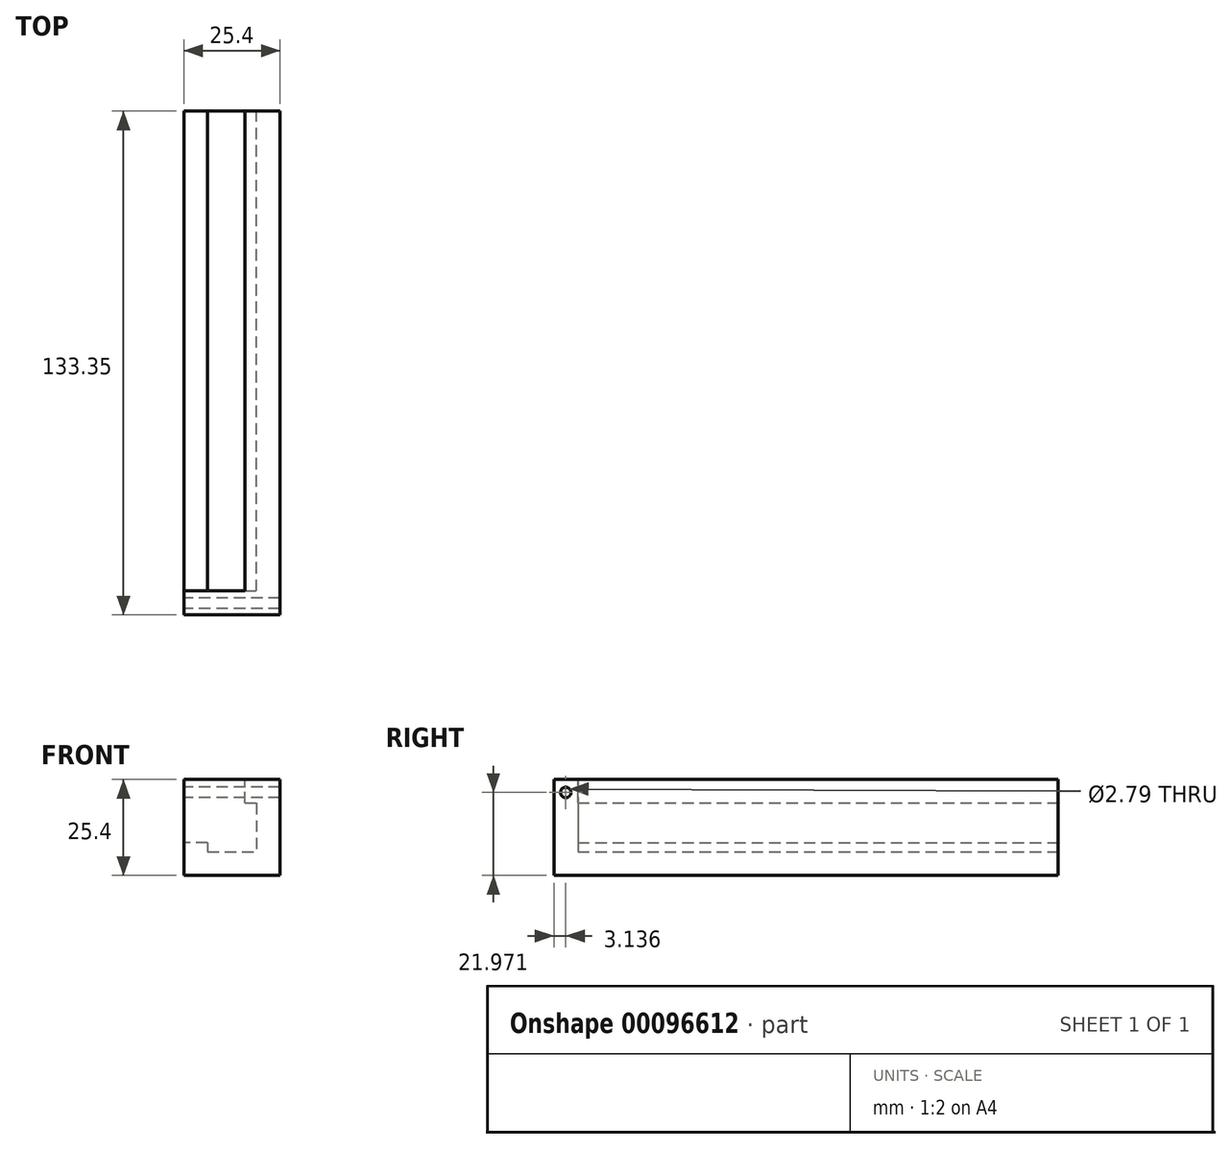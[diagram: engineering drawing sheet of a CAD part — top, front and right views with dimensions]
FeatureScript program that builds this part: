
annotation { "Feature Type Name" : "Feature", "Feature Type Description" : "" }
export const myFeature = defineFeature(function(context is Context, id is Id, definition is map)
    precondition{}
    {
        {
            var Q0;
            Q0=qCreatedBy(makeId("Front.planeOp"),FACE);
            var sketch = newSketch(context, id + "F0", { "sketchPlane" : qUnion([Q0])});
            skLineSegment(sketch, "E0.bottom", {"start": v(-12.7, 12.7) * mm, "end": v(12.7, 12.7) * mm});
            skLineSegment(sketch, "E0.top", {"start": v(-12.7, -12.7) * mm, "end": v(12.7, -12.7) * mm});
            skLineSegment(sketch, "E0.left", {"start": v(-12.7, 12.7) * mm, "end": v(-12.7, -12.7) * mm});
            skLineSegment(sketch, "E0.right", {"start": v(12.7, 12.7) * mm, "end": v(12.7, -12.7) * mm});
            skPoint(sketch, "E0.middle", {"position": v(0, 0) * mm});
            skLineSegment(sketch, "E1.bottom", {"start": v(-6.48, 6.48) * mm, "end": v(6.48, 6.48) * mm});
            skLineSegment(sketch, "E1.top", {"start": v(-6.48, -6.48) * mm, "end": v(6.48, -6.48) * mm});
            skLineSegment(sketch, "E1.left", {"start": v(-6.48, 6.48) * mm, "end": v(-6.48, -6.48) * mm});
            skLineSegment(sketch, "E1.right", {"start": v(6.48, 6.48) * mm, "end": v(6.48, -6.48) * mm});
            skLineSegment(sketch, "E2", {"start": v(3.39, 6.48) * mm, "end": v(3.39, 12.7) * mm});
            skLineSegment(sketch, "E3", {"start": v(3.39, 12.7) * mm, "end": v(3.39, 6.48) * mm});
            skLineSegment(sketch, "E4", {"start": v(-6.48, -4.04) * mm, "end": v(-12.7, -4.04) * mm});
            skLineSegment(sketch, "E5", {"start": v(-12.7, -4.04) * mm, "end": v(-6.48, -4.04) * mm});
            skSolve(sketch);
        }
        {
            var Q0;
            {var subQ3=sQuery(id+"F0.wireOp",EDGE,"E0.top");Q0=makeQuery(id+"F0.imprint","IMPRINT",FACE,{"disambiguationData":[TD([[makeQuery(id+"F0.imprint","IMPRINT",EDGE,{"derivedFrom":subQ3}),1.0]])]});}
            extrude(context, id + "F1", {"entities" : qUnion([Q0]), "depth" : 127 * mm});
        }
        {
            var Q0;
            Q0=makeQuery(id+"F1.opExtrude","CAP_FACE",FACE,{"disambiguationData":[OSD([sQuery(id+"F0.wireOp",EDGE,"E0.bottom"),sQuery(id+"F0.wireOp",EDGE,"E0.top"),sQuery(id+"F0.wireOp",EDGE,"E0.left"),sQuery(id+"F0.wireOp",EDGE,"E0.right"),sQuery(id+"F0.wireOp",EDGE,"E1.bottom"),sQuery(id+"F0.wireOp",EDGE,"E1.top"),sQuery(id+"F0.wireOp",EDGE,"E1.left"),sQuery(id+"F0.wireOp",EDGE,"E1.right"),sQuery(id+"F0.wireOp",EDGE,"E3"),sQuery(id+"F0.wireOp",EDGE,"E5")])],"isStart":false});
            var sketch = newSketch(context, id + "F2", { "sketchPlane" : qUnion([Q0])});
            skLineSegment(sketch, "E6.bottom", {"start": v(12.7, -12.7) * mm, "end": v(-12.7, -12.7) * mm});
            skLineSegment(sketch, "E6.top", {"start": v(12.7, 12.7) * mm, "end": v(-12.7, 12.7) * mm});
            skLineSegment(sketch, "E6.left", {"start": v(12.7, -12.7) * mm, "end": v(12.7, 12.7) * mm});
            skLineSegment(sketch, "E6.right", {"start": v(-12.7, -12.7) * mm, "end": v(-12.7, 12.7) * mm});
            skSolve(sketch);
        }
        {
            var Q0;
            Q0 = qSketchRegion(id + "F2", true);
            extrude(context, id + "F3", {"entities" : qUnion([Q0]), "operationType" : NewBodyOperationType.ADD, "depth" : 6.35 * mm});
        }
        {
            var Q0;
            Q0=makeQuery(id+"F3.boolean.opBoolean","MERGE",FACE,{"derivedFrom":[makeQuery(id+"F1.opExtrude","SWEPT_FACE",FACE,{"disambiguationData":[OSD([sQuery(id+"F0.wireOp",EDGE,"E0.left")])]}),makeQuery(id+"F3.opExtrude","SWEPT_FACE",FACE,{"disambiguationData":[OSD([sQuery(id+"F2.wireOp",EDGE,"E6.right")])]})]});
            var sketch = newSketch(context, id + "F4", { "sketchPlane" : qUnion([Q0])});
            skCircle(sketch, "E7", {"center": v(130.21, 9.27) * mm, "radius": 1.4 * mm});
            skSolve(sketch);
        }
        {
            var Q0;
            Q0 = qSketchRegion(id + "F4", true);
            extrude(context, id + "F5", {"entities" : qUnion([Q0]), "operationType" : NewBodyOperationType.REMOVE, "endBound" : BoundingType.THROUGH_ALL, "oppositeDirection" : true, "depth" : 25.4 * mm});
        }
    });
